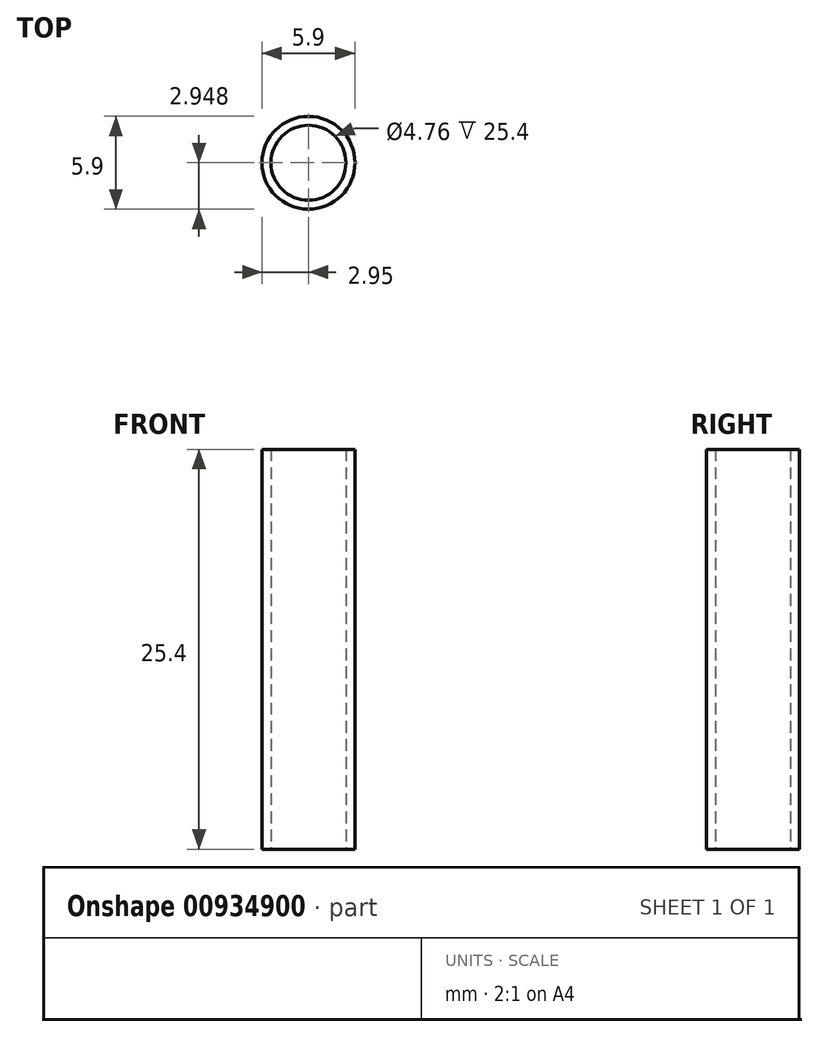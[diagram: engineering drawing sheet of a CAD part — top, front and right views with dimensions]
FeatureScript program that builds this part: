
annotation { "Feature Type Name" : "Feature", "Feature Type Description" : "" }
export const myFeature = defineFeature(function(context is Context, id is Id, definition is map)
    precondition{}
    {
        {
            var Q0;
            Q0=qCreatedBy(makeId("Top.planeOp"),FACE);
            var sketch = newSketch(context, id + "F0", { "sketchPlane" : qUnion([Q0])});
            skCircle(sketch, "E0", {"center": v(0, -13.88) * mm, "radius": 2.95 * mm});
            skCircle(sketch, "E1", {"center": v(0, -13.88) * mm, "radius": 2.38 * mm});
            skSolve(sketch);
        }
        {
            var Q0;
            Q0 = qSketchRegion(id + "F0", true);
            extrude(context, id + "F1", {"entities" : qUnion([Q0]), "depth" : 25.4 * mm, "offsetDistance" : 25.4 * mm});
        }
    });
